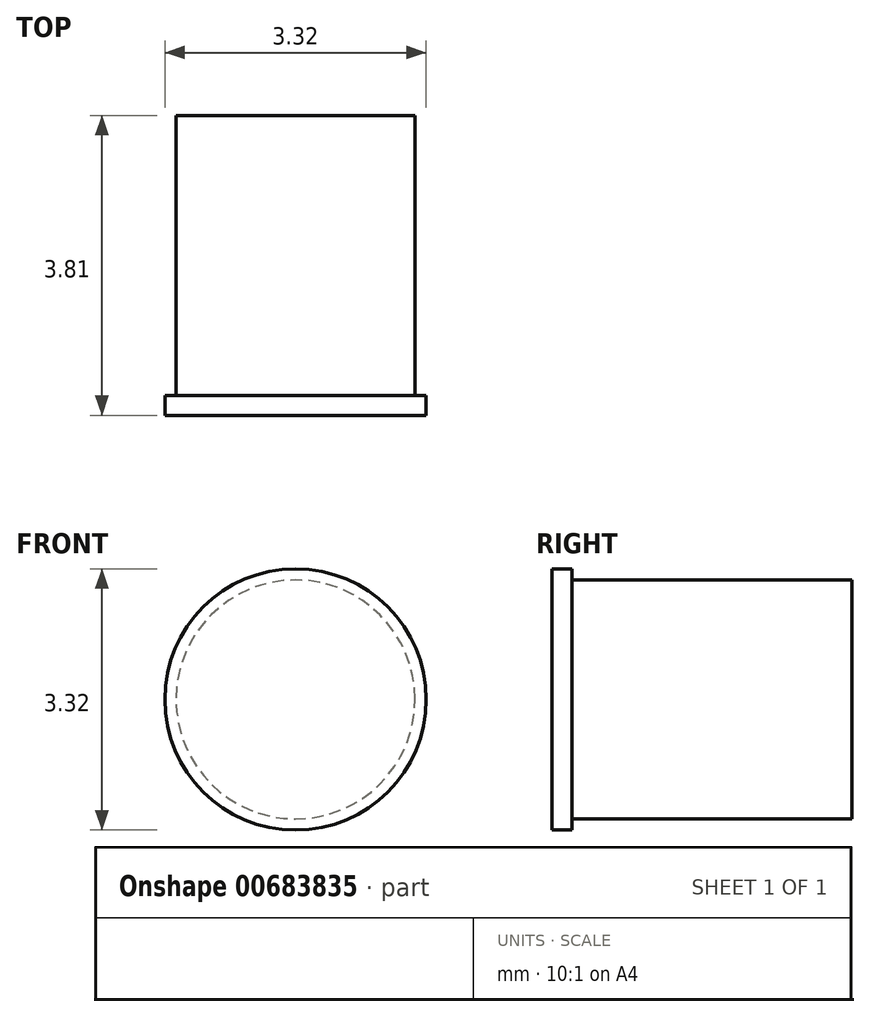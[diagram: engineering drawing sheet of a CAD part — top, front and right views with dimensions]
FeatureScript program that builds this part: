
annotation { "Feature Type Name" : "Feature", "Feature Type Description" : "" }
export const myFeature = defineFeature(function(context is Context, id is Id, definition is map)
    precondition{}
    {
        {
            var Q0;
            Q0=qCreatedBy(makeId("Front.planeOp"),FACE);
            var sketch = newSketch(context, id + "F0", { "sketchPlane" : qUnion([Q0])});
            skCircle(sketch, "E0", {"center": v(0, 0) * mm, "radius": 1.52 * mm});
            skSolve(sketch);
        }
        {
            var Q0;
            Q0=makeQuery(id+"F0.imprint","IMPRINT",FACE,{"disambiguationData":[TD([[makeQuery(id+"F0.imprint","IMPRINT",EDGE,{"derivedFrom":sQuery(id+"F0.wireOp",EDGE,"E0")}),1.0]])]});
            extrude(context, id + "F1", {"entities" : qUnion([Q0]), "depth" : 1.78 * mm, "offsetDistance" : 25.4 * mm, "hasSecondDirection" : true, "secondDirectionOppositeDirection" : true, "secondDirectionDepth" : 1.78 * mm});
        }
        {
            var Q0;
            Q0=makeQuery(id+"F1.opExtrude","CAP_FACE",FACE,{"disambiguationData":[OSD([sQuery(id+"F0.wireOp",EDGE,"E0")])],"isStart":false});
            var sketch = newSketch(context, id + "F2", { "sketchPlane" : qUnion([Q0])});
            skCircle(sketch, "E1", {"center": v(0, 0) * mm, "radius": 1.66 * mm});
            skSolve(sketch);
        }
        {
            var Q0;
            Q0 = qSketchRegion(id + "F2", true);
            extrude(context, id + "F3", {"entities" : qUnion([Q0]), "operationType" : NewBodyOperationType.ADD, "depth" : 0.25 * mm, "offsetDistance" : 25.4 * mm});
        }
    });
